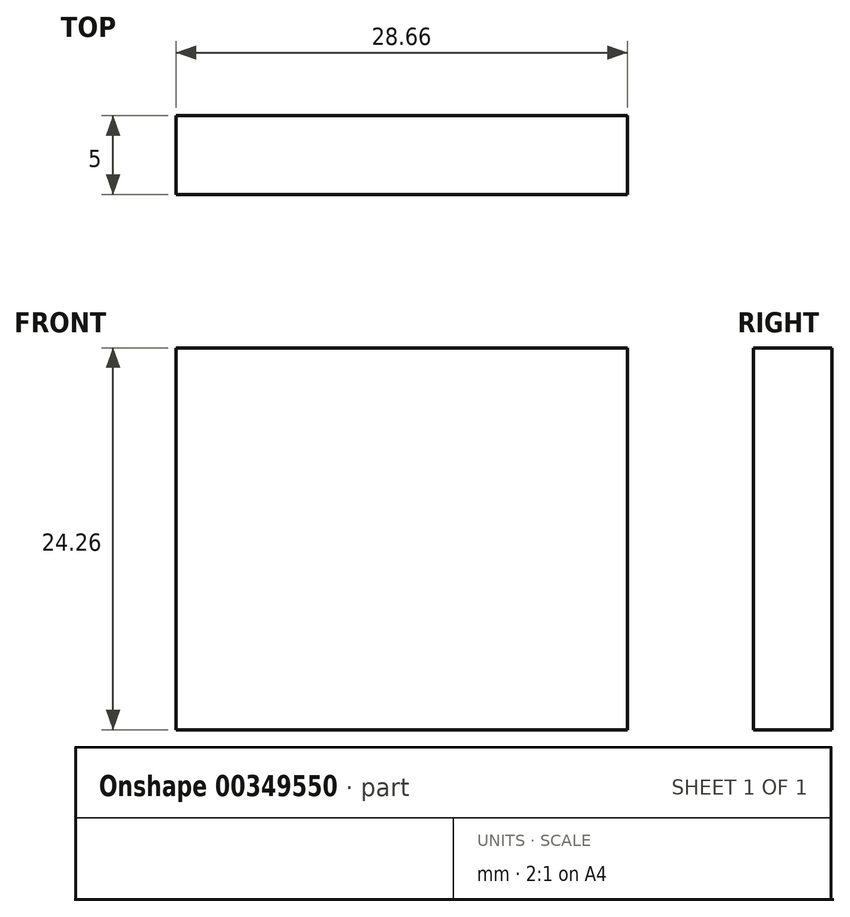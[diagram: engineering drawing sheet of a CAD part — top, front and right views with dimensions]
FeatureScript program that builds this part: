
annotation { "Feature Type Name" : "Feature", "Feature Type Description" : "" }
export const myFeature = defineFeature(function(context is Context, id is Id, definition is map)
    precondition{}
    {
        {
            var Q0;
            Q0=qCreatedBy(makeId("Front.planeOp"),FACE);
            var sketch = newSketch(context, id + "F0", { "sketchPlane" : qUnion([Q0])});
            skLineSegment(sketch, "E0.bottom", {"start": v(-28.66, -24.26) * mm, "end": v(0, -24.26) * mm});
            skLineSegment(sketch, "E0.top", {"start": v(-28.66, 0) * mm, "end": v(0, 0) * mm});
            skLineSegment(sketch, "E0.left", {"start": v(-28.66, -24.26) * mm, "end": v(-28.66, 0) * mm});
            skLineSegment(sketch, "E0.right", {"start": v(0, -24.26) * mm, "end": v(0, 0) * mm});
            skSolve(sketch);
        }
        {
            var Q0;
            Q0=makeQuery(id+"F0.imprint","IMPRINT",FACE,{"disambiguationData":[TD([[makeQuery(id+"F0.imprint","IMPRINT",EDGE,{"derivedFrom":sQuery(id+"F0.wireOp",EDGE,"E0.bottom")}),1.0]])]});
            extrude(context, id + "F1", {"entities" : qUnion([Q0]), "depth" : 5 * mm});
        }
    });
